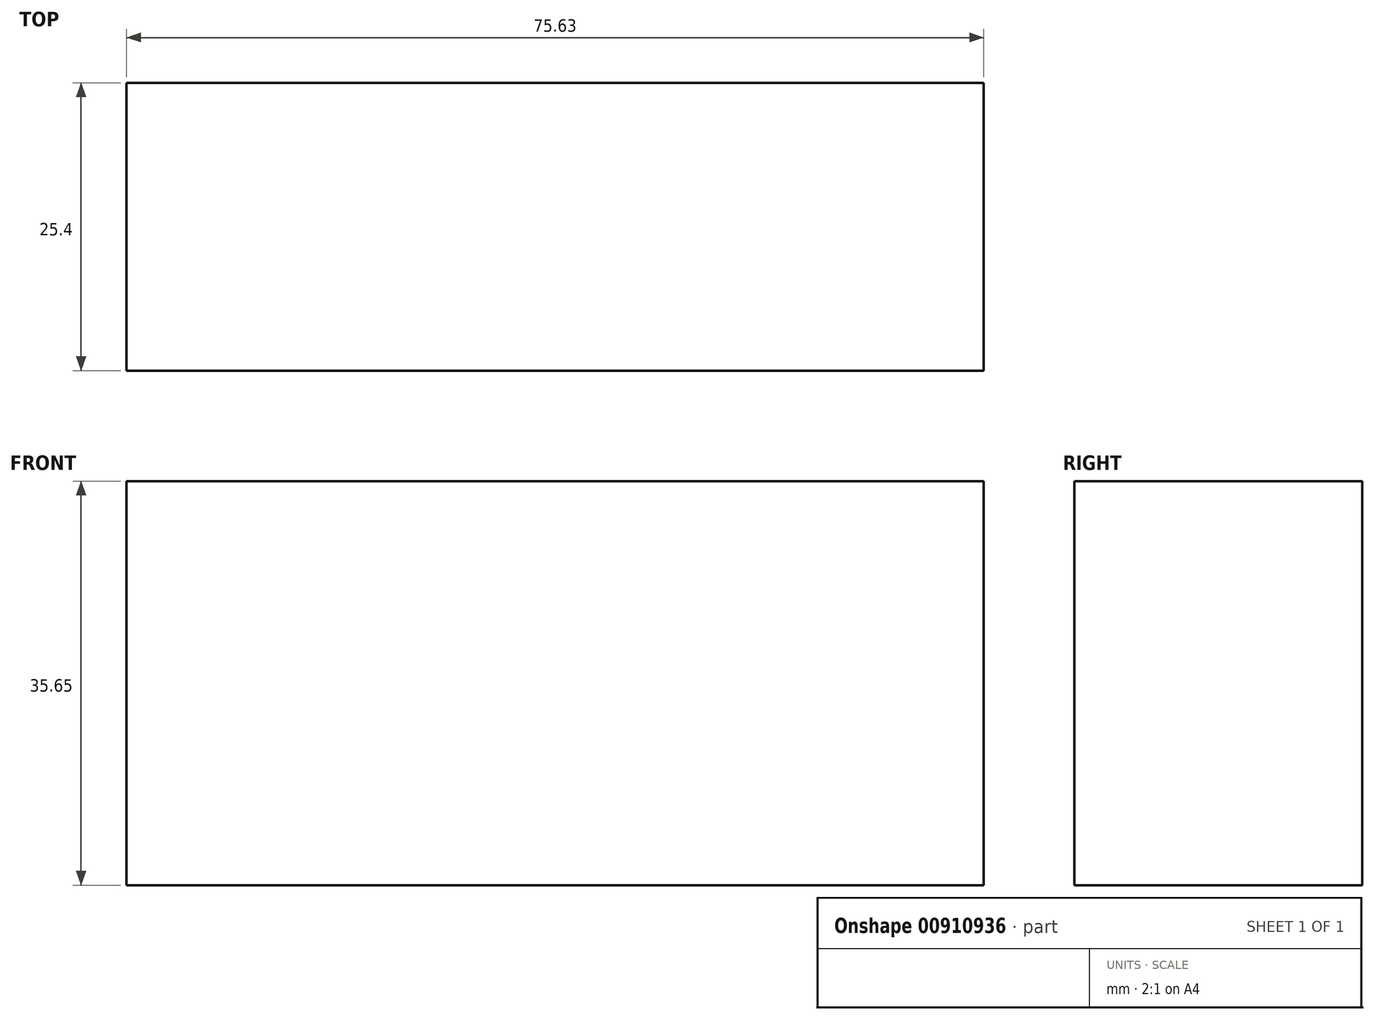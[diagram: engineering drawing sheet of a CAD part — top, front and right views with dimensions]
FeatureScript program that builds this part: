
annotation { "Feature Type Name" : "Feature", "Feature Type Description" : "" }
export const myFeature = defineFeature(function(context is Context, id is Id, definition is map)
    precondition{}
    {
        {
            var Q0;
            Q0=qCreatedBy(makeId("Front.planeOp"),FACE);
            var sketch = newSketch(context, id + "F0", { "sketchPlane" : qUnion([Q0])});
            skLineSegment(sketch, "E0.bottom", {"start": v(-75.63, 35.65) * mm, "end": v(0, 35.65) * mm});
            skLineSegment(sketch, "E0.top", {"start": v(-75.63, 0) * mm, "end": v(0, 0) * mm});
            skLineSegment(sketch, "E0.left", {"start": v(-75.63, 35.65) * mm, "end": v(-75.63, 0) * mm});
            skLineSegment(sketch, "E0.right", {"start": v(0, 35.65) * mm, "end": v(0, 0) * mm});
            skSolve(sketch);
        }
        {
            var Q0;
            Q0 = qSketchRegion(id + "F0", true);
            extrude(context, id + "F1", {"entities" : qUnion([Q0]), "depth" : 25.4 * mm, "offsetDistance" : 25.4 * mm});
        }
    });
